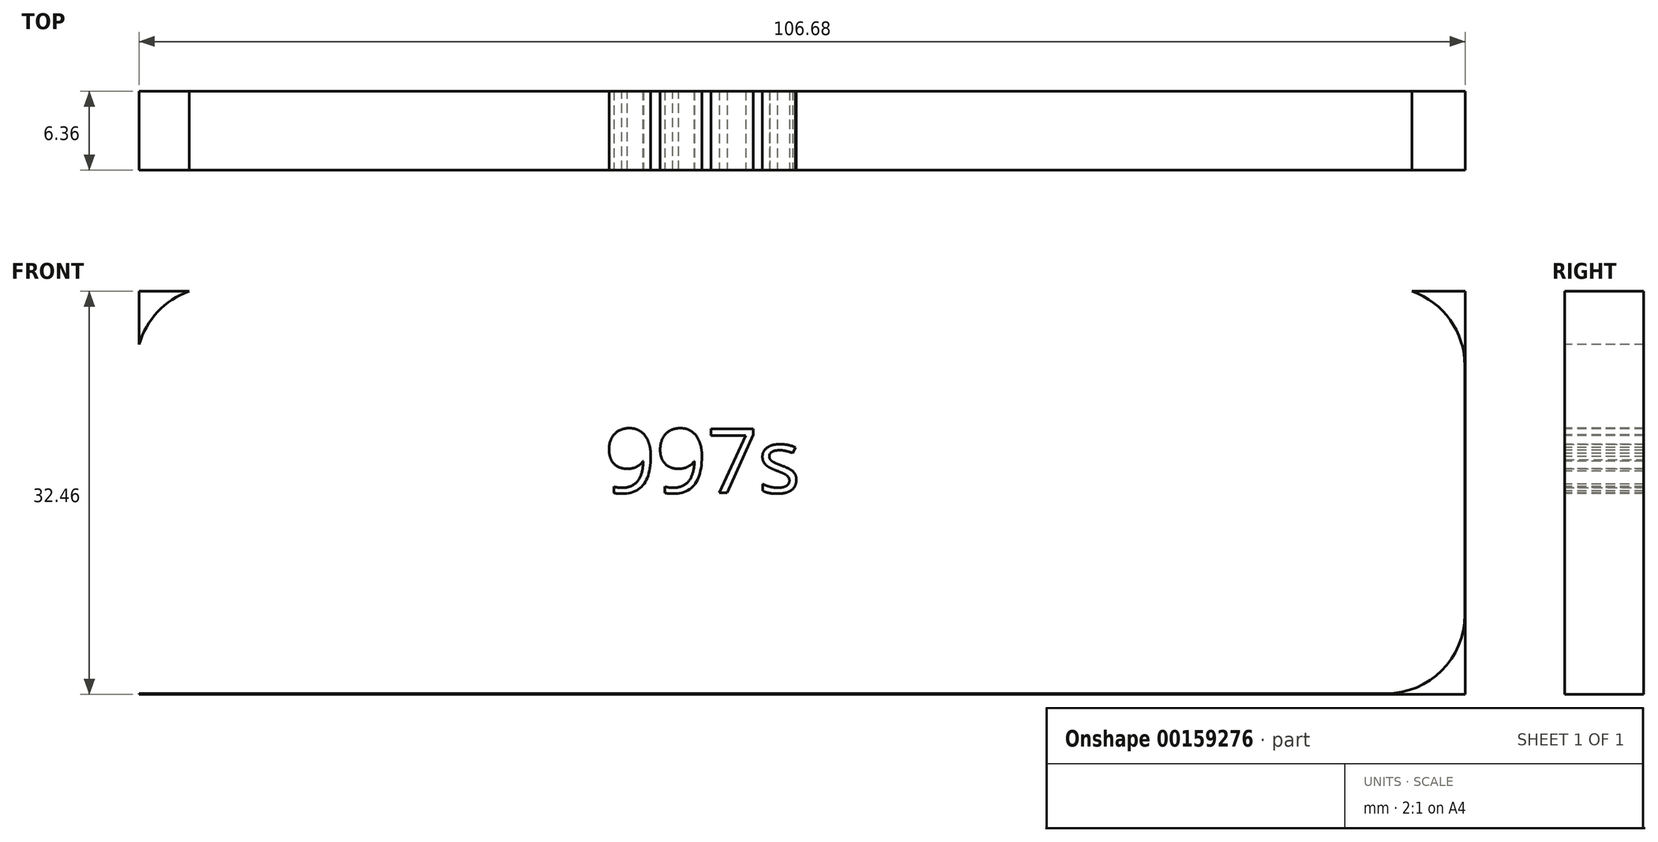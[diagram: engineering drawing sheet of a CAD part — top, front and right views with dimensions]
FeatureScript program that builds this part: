
annotation { "Feature Type Name" : "Feature", "Feature Type Description" : "" }
export const myFeature = defineFeature(function(context is Context, id is Id, definition is map)
    precondition{}
    {
        {
            var Q0;
            Q0=qCreatedBy(makeId("Front.planeOp"),FACE);
            var sketch = newSketch(context, id + "F0", { "sketchPlane" : qUnion([Q0])});
            skLineSegment(sketch, "E0.bottom", {"start": v(53.34, -16.23) * mm, "end": v(-53.34, -16.23) * mm});
            skLineSegment(sketch, "E0.top", {"start": v(53.34, 16.23) * mm, "end": v(-53.34, 16.23) * mm});
            skLineSegment(sketch, "E0.left", {"start": v(53.34, -16.23) * mm, "end": v(53.34, 16.23) * mm});
            skLineSegment(sketch, "E0.right", {"start": v(-53.34, -16.23) * mm, "end": v(-53.34, 16.23) * mm});
            skPoint(sketch, "E0.middle", {"position": v(0, 0) * mm});
            skCircle(sketch, "E1", {"center": v(-36.42, 0) * mm, "radius": 4.33 * mm});
            skCircle(sketch, "E2", {"center": v(28.48, 0) * mm, "radius": 4.49 * mm});
            skSolve(sketch);
        }
        {
            var Q0;
            Q0=qCreatedBy(makeId("Front.planeOp"),FACE);
            var sketch = newSketch(context, id + "F1", { "sketchPlane" : qUnion([Q0])});
            skLineSegment(sketch, "E3.bottom", {"start": v(-53.44, 0) * mm, "end": v(-83.92, 0) * mm});
            skLineSegment(sketch, "E3.top", {"start": v(-53.44, -16.17) * mm, "end": v(-90.27, -16.17) * mm});
            skLineSegment(sketch, "E3.right", {"start": v(-90.27, -6.35) * mm, "end": v(-90.27, -16.17) * mm});
            skLineSegment(sketch, "E4", {"start": v(-90.27, -16.17) * mm, "end": v(46.96, -16.17) * mm});
            skLineSegment(sketch, "E5", {"start": v(53.3, -9.82) * mm, "end": v(53.3, 10.23) * mm});
            skLineSegment(sketch, "E6", {"start": v(46.96, 16.58) * mm, "end": v(-47.22, 16.58) * mm});
            skLineSegment(sketch, "E7", {"start": v(-53.57, 10.15) * mm, "end": v(-53.44, 0) * mm});
            skPoint(sketch, "E8.visualSharp", {"position": v(-53.65, 16.58) * mm});
            skArc(sketch, "E8.filletArc", {"start": v(-47.22, 16.58) * mm, "mid": v(-51.74, 14.7) * mm, "end": v(-53.57, 10.15) * mm});
            skPoint(sketch, "E9.visualSharp", {"position": v(53.3, 16.58) * mm});
            skArc(sketch, "E9.filletArc", {"start": v(53.3, 10.23) * mm, "mid": v(51.45, 14.72) * mm, "end": v(46.96, 16.58) * mm});
            skPoint(sketch, "E10.visualSharp", {"position": v(53.3, -16.17) * mm});
            skArc(sketch, "E10.filletArc", {"start": v(46.96, -16.17) * mm, "mid": v(51.45, -14.3) * mm, "end": v(53.3, -9.82) * mm});
            skPoint(sketch, "E11.visualSharp", {"position": v(-90.27, 0) * mm});
            skArc(sketch, "E11.filletArc", {"start": v(-83.92, 0) * mm, "mid": v(-88.41, -1.86) * mm, "end": v(-90.27, -6.35) * mm});
            skText(sketch, "E12", { "text": "997s", "fontName": "OpenSans-Regular.ttf"});
            const initialGuessF1  = {"E12": [-0.01591, 0, 1, 0, 0.00518]};
            skSetInitialGuess(sketch, initialGuessF1);
            skSolve(sketch);
        }
        {
            var Q0;
            Q0=qCreatedBy(makeId("Front.planeOp"),FACE);
            var sketch = newSketch(context, id + "F2", { "sketchPlane" : qUnion([Q0])});
            skCircle(sketch, "E13", {"center": v(-81.86, -7.26) * mm, "radius": 3.18 * mm});
            skCircle(sketch, "E14", {"center": v(-64.56, -7.05) * mm, "radius": 3.18 * mm});
            skSolve(sketch);
        }
        {
            var Q0;
            Q0=makeQuery(id+"F0.imprint","IMPRINT",FACE,{"disambiguationData":[TD([[makeQuery(id+"F0.imprint","IMPRINT",EDGE,{"derivedFrom":sQuery(id+"F0.wireOp",EDGE,"E0.bottom")}),-1.0]])]});
            var Q1;
            Q1=makeQuery(id+"F2.imprint","IMPRINT",FACE,{"disambiguationData":[TD([[makeQuery(id+"F2.imprint","IMPRINT",EDGE,{"derivedFrom":sQuery(id+"F2.wireOp",EDGE,"E14")}),1.0]])]});
            var Q2;
            Q2=makeQuery(id+"F2.imprint","IMPRINT",FACE,{"disambiguationData":[TD([[makeQuery(id+"F2.imprint","IMPRINT",EDGE,{"derivedFrom":sQuery(id+"F2.wireOp",EDGE,"E13")}),1.0]])]});
            var Q3;
            Q3=makeQuery(id+"F1.imprint","IMPRINT",FACE,{"disambiguationData":[TD([[makeQuery(id+"F1.imprint","IMPRINT",EDGE,{"derivedFrom":sQuery(id+"F1.wireOp",EDGE,"E3.bottom")}),1.0]])]});
            extrude(context, id + "F3", {"entities" : qUnion([Q0, Q1, Q2, Q3]), "endBound" : BoundingType.SYMMETRIC, "depth" : 6.35 * mm});
        }
        {
            var Q0;
            Q0=makeQuery(id+"F3.opExtrude","CAP_FACE",FACE,{"disambiguationData":[OSD([sQuery(id+"F2.wireOp",EDGE,"E13")])],"isStart":false});
            extrude(context, id + "F4", {"entities" : qUnion([Q0]), "endBound" : BoundingType.SYMMETRIC, "depth" : 0.03 * mm});
        }
        {
            var Q0;
            Q0=makeQuery(id+"F4.opExtrude","CAP_FACE",FACE,{"disambiguationData":[OSD([sQuery(id+"F2.wireOp",EDGE,"E13")])],"isStart":false});
            var Q1;
            Q1=makeQuery(id+"F3.opExtrude","CAP_FACE",FACE,{"disambiguationData":[OSD([sQuery(id+"F1.wireOp",EDGE,"E3.bottom"),sQuery(id+"F1.wireOp",EDGE,"E3.right"),sQuery(id+"F1.wireOp",EDGE,"E4"),sQuery(id+"F1.wireOp",EDGE,"E5"),sQuery(id+"F1.wireOp",EDGE,"E6"),sQuery(id+"F1.wireOp",EDGE,"E7"),sQuery(id+"F1.wireOp",EDGE,"E8.filletArc"),sQuery(id+"F1.wireOp",EDGE,"E9.filletArc"),sQuery(id+"F1.wireOp",EDGE,"E10.filletArc"),sQuery(id+"F1.wireOp",EDGE,"E11.filletArc"),sQuery(id+"F1.wireOp",EDGE,"E12.sketch_text.stroke-0"),sQuery(id+"F1.wireOp",EDGE,"E12.sketch_text.stroke-1"),sQuery(id+"F1.wireOp",EDGE,"E12.sketch_text.stroke-2"),sQuery(id+"F1.wireOp",EDGE,"E12.sketch_text.stroke-3"),sQuery(id+"F1.wireOp",EDGE,"E12.sketch_text.stroke-4"),sQuery(id+"F1.wireOp",EDGE,"E12.sketch_text.stroke-5"),sQuery(id+"F1.wireOp",EDGE,"E12.sketch_text.stroke-6"),sQuery(id+"F1.wireOp",EDGE,"E12.sketch_text.stroke-7"),sQuery(id+"F1.wireOp",EDGE,"E12.sketch_text.stroke-8"),sQuery(id+"F1.wireOp",EDGE,"E12.sketch_text.stroke-9"),sQuery(id+"F1.wireOp",EDGE,"E12.sketch_text.stroke-10"),sQuery(id+"F1.wireOp",EDGE,"E12.sketch_text.stroke-11"),sQuery(id+"F1.wireOp",EDGE,"E12.sketch_text.stroke-12"),sQuery(id+"F1.wireOp",EDGE,"E12.sketch_text.stroke-13"),sQuery(id+"F1.wireOp",EDGE,"E12.sketch_text.stroke-14"),sQuery(id+"F1.wireOp",EDGE,"E12.sketch_text.stroke-15"),sQuery(id+"F1.wireOp",EDGE,"E12.sketch_text.stroke-26"),sQuery(id+"F1.wireOp",EDGE,"E12.sketch_text.stroke-27"),sQuery(id+"F1.wireOp",EDGE,"E12.sketch_text.stroke-28"),sQuery(id+"F1.wireOp",EDGE,"E12.sketch_text.stroke-29"),sQuery(id+"F1.wireOp",EDGE,"E12.sketch_text.stroke-30"),sQuery(id+"F1.wireOp",EDGE,"E12.sketch_text.stroke-31"),sQuery(id+"F1.wireOp",EDGE,"E12.sketch_text.stroke-32"),sQuery(id+"F1.wireOp",EDGE,"E12.sketch_text.stroke-33"),sQuery(id+"F1.wireOp",EDGE,"E12.sketch_text.stroke-34"),sQuery(id+"F1.wireOp",EDGE,"E12.sketch_text.stroke-35"),sQuery(id+"F1.wireOp",EDGE,"E12.sketch_text.stroke-36"),sQuery(id+"F1.wireOp",EDGE,"E12.sketch_text.stroke-37"),sQuery(id+"F1.wireOp",EDGE,"E12.sketch_text.stroke-38"),sQuery(id+"F1.wireOp",EDGE,"E12.sketch_text.stroke-39"),sQuery(id+"F1.wireOp",EDGE,"E12.sketch_text.stroke-40"),sQuery(id+"F1.wireOp",EDGE,"E12.sketch_text.stroke-41"),sQuery(id+"F1.wireOp",EDGE,"E12.sketch_text.stroke-52"),sQuery(id+"F1.wireOp",EDGE,"E12.sketch_text.stroke-53"),sQuery(id+"F1.wireOp",EDGE,"E12.sketch_text.stroke-54"),sQuery(id+"F1.wireOp",EDGE,"E12.sketch_text.stroke-55"),sQuery(id+"F1.wireOp",EDGE,"E12.sketch_text.stroke-56"),sQuery(id+"F1.wireOp",EDGE,"E12.sketch_text.stroke-57"),sQuery(id+"F1.wireOp",EDGE,"E12.sketch_text.stroke-58"),sQuery(id+"F1.wireOp",EDGE,"E12.sketch_text.stroke-59"),sQuery(id+"F1.wireOp",EDGE,"E12.sketch_text.stroke-60"),sQuery(id+"F1.wireOp",EDGE,"E12.sketch_text.stroke-61"),sQuery(id+"F1.wireOp",EDGE,"E12.sketch_text.stroke-62"),sQuery(id+"F1.wireOp",EDGE,"E12.sketch_text.stroke-63"),sQuery(id+"F1.wireOp",EDGE,"E12.sketch_text.stroke-64"),sQuery(id+"F1.wireOp",EDGE,"E12.sketch_text.stroke-65"),sQuery(id+"F1.wireOp",EDGE,"E12.sketch_text.stroke-66"),sQuery(id+"F1.wireOp",EDGE,"E12.sketch_text.stroke-67"),sQuery(id+"F1.wireOp",EDGE,"E12.sketch_text.stroke-68"),sQuery(id+"F1.wireOp",EDGE,"E12.sketch_text.stroke-69"),sQuery(id+"F1.wireOp",EDGE,"E12.sketch_text.stroke-70"),sQuery(id+"F1.wireOp",EDGE,"E12.sketch_text.stroke-71"),sQuery(id+"F1.wireOp",EDGE,"E12.sketch_text.stroke-72"),sQuery(id+"F1.wireOp",EDGE,"E12.sketch_text.stroke-73"),sQuery(id+"F1.wireOp",EDGE,"E12.sketch_text.stroke-74"),sQuery(id+"F1.wireOp",EDGE,"E12.sketch_text.stroke-75"),sQuery(id+"F1.wireOp",EDGE,"E12.sketch_text.stroke-76"),sQuery(id+"F1.wireOp",EDGE,"E12.sketch_text.stroke-77"),sQuery(id+"F1.wireOp",EDGE,"E12.sketch_text.stroke-78"),sQuery(id+"F1.wireOp",EDGE,"E12.sketch_text.stroke-79"),sQuery(id+"F1.wireOp",EDGE,"E12.sketch_text.stroke-80"),sQuery(id+"F1.wireOp",EDGE,"E12.sketch_text.stroke-81"),sQuery(id+"F1.wireOp",EDGE,"E12.sketch_text.stroke-82"),sQuery(id+"F1.wireOp",EDGE,"E12.sketch_text.stroke-83")])],"isStart":false});
            extrude(context, id + "F5", {"entities" : qUnion([Q0, Q1]), "operationType" : NewBodyOperationType.REMOVE, "oppositeDirection" : true, "depth" : 25.4 * mm});
        }
    });
